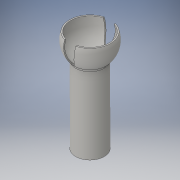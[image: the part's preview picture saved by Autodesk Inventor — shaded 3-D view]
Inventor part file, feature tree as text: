
AUTODESK INVENTOR PART (.ipt)
format: ipt  version: 2016 (Build 200138000, 138)  size: 198,144 bytes
history: native  units: in
note: dims shown in document units (in); Inventor stores cm internally (conversion verified against a paired STEP export)
features: sketch x14, plane x4, extrude x3, revolve x3, fillet x1
ambient origin geometry x8: Origin, YZ Plane, XZ Plane, XY Plane, X Axis, Y Axis, Z Axis, Center Point
bodies: Solid1 (feature_tree)
feature tree (25):
  extrude  "Extrusion1"  Depth=0.3in
  sketch  "3D Sketch1"
  sketch  "Sketch2"  dims[d3=0.74in d4=180.0deg]
  sketch  "Sketch3"  dims[d5=0.687in d6=0.7in]
  sketch  "Sketch4"  dims[d7=180.0deg d8=0.42in]
  sketch  "Sketch5"  dims[d9=1.0in d10=0.0in d11=1.0in d12=0.0in]
  plane  "Work Plane1"
  revolve  "Revolution1"  Angle=180.0deg
  revolve  "Revolution2"  [1 undecoded]
  sketch  "Sketch8"  dims[d24=0.25in]
  plane  "Work Plane2"
  extrude  "Extrusion2"  Depth=0.42in
  extrude  "Extrusion3"  Depth=1.0in TaperAngle=0.0deg
  sketch  "Sketch11"  dims[d27=90.0deg]
  plane  "Work Plane3"
  sketch  "Sketch13"  dims[d28=0.125in]
  plane  "Work Plane4"
  revolve  "Revolution3"  [1 undecoded]
  fillet  "Fillet1"  [1 undecoded]
  sketch  "Sketch1"  dims[d0=1.3in d1=0.0in d2=0.3in]
  sketch  "Sketch6"  dims[d13=0.236in d14=-0.088in d22=0.0in]
  sketch  "Sketch7"  dims[d23=0.118in]
  sketch  "Sketch9"  dims[d25=0.113in]
  sketch  "Sketch10"  dims[d26=0.065in]
  sketch  "Sketch14"
note: 3 required parameter values undecoded (feature->parameter linkage not recoverable at this tier; creation-order binding heuristic only, values carry confidence <= 0.55)